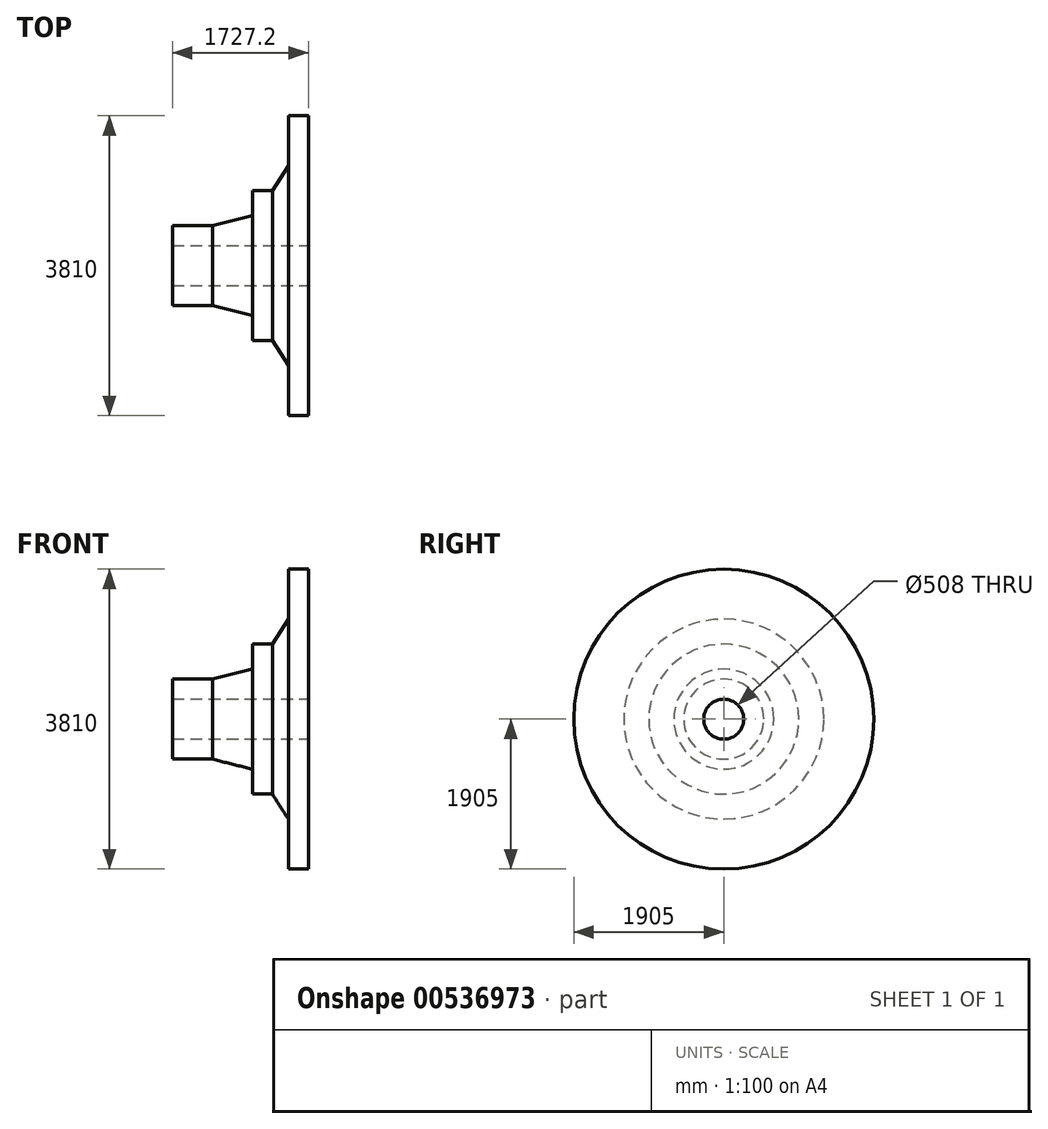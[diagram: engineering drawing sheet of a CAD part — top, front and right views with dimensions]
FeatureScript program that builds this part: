
annotation { "Feature Type Name" : "Feature", "Feature Type Description" : "" }
export const myFeature = defineFeature(function(context is Context, id is Id, definition is map)
    precondition{}
    {
        {
            var Q0;
            Q0=qCreatedBy(makeId("Front.planeOp"),FACE);
            var sketch = newSketch(context, id + "F0", { "sketchPlane" : qUnion([Q0])});
            skLineSegment(sketch, "E0", {"start": v(812.28, -641.5) * mm, "end": v(-914.92, -641.5) * mm});
            skLineSegment(sketch, "E1", {"start": v(-914.92, -641.5) * mm, "end": v(-914.92, -387.5) * mm});
            skLineSegment(sketch, "E2", {"start": v(-914.92, -387.5) * mm, "end": v(-406.92, -387.5) * mm});
            skLineSegment(sketch, "E3", {"start": v(-406.92, -387.5) * mm, "end": v(101.08, -260.5) * mm});
            skLineSegment(sketch, "E4", {"start": v(101.08, -260.5) * mm, "end": v(101.08, 57) * mm});
            skLineSegment(sketch, "E5", {"start": v(101.08, 57) * mm, "end": v(355.08, 57) * mm});
            skLineSegment(sketch, "E6", {"start": v(355.08, 57) * mm, "end": v(558.28, 374.5) * mm});
            skLineSegment(sketch, "E7", {"start": v(558.28, 374.5) * mm, "end": v(558.28, 1009.5) * mm});
            skLineSegment(sketch, "E8", {"start": v(558.28, 1009.5) * mm, "end": v(812.28, 1009.5) * mm});
            skLineSegment(sketch, "E9", {"start": v(812.28, 1009.5) * mm, "end": v(812.28, -641.5) * mm});
            skLineSegment(sketch, "E10", {"start": v(823.84, -895.5) * mm, "end": v(-1059.9, -895.5) * mm});
            skSolve(sketch);
        }
        {
            var Q0;
            Q0=makeQuery(id+"F0.imprint","IMPRINT",FACE,{"disambiguationData":[TD([[makeQuery(id+"F0.imprint","IMPRINT",EDGE,{"derivedFrom":sQuery(id+"F0.wireOp",EDGE,"E0")}),-1.0]])]});
            var Q1;
            Q1=sQuery(id+"F0.wireOp",EDGE,"E10");
            revolve(context, id + "F1", {"entities" : qUnion([Q0]), "axis" : qUnion([Q1]), "revolveType" : RevolveType.FULL});
        }
    });
